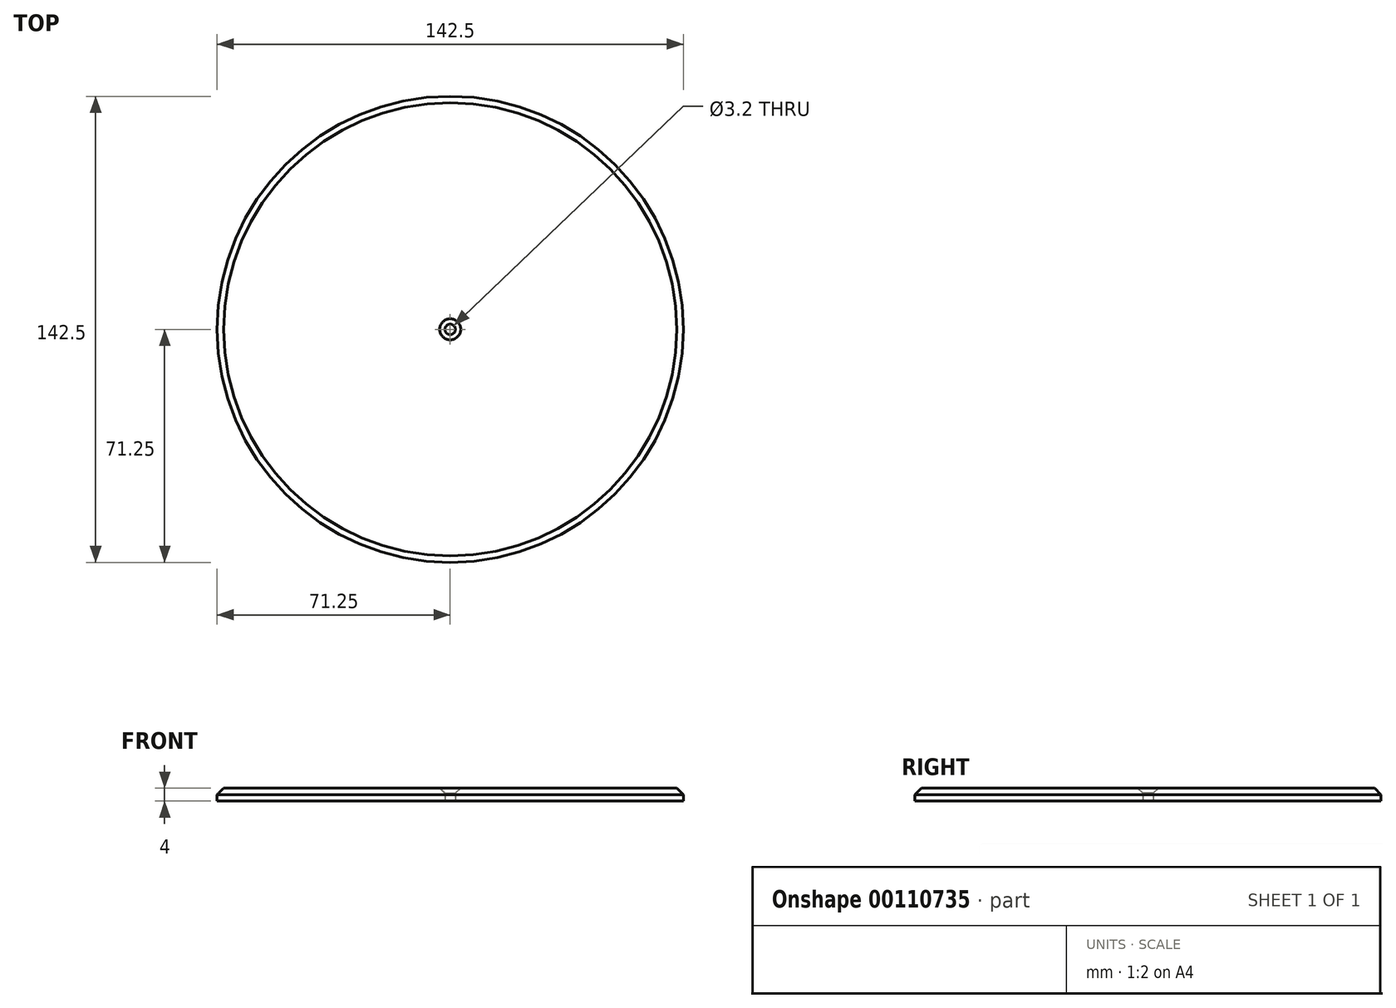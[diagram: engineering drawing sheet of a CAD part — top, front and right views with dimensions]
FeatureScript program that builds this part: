
annotation { "Feature Type Name" : "Feature", "Feature Type Description" : "" }
export const myFeature = defineFeature(function(context is Context, id is Id, definition is map)
    precondition{}
    {
        {
            var Q0;
            Q0=qCreatedBy(makeId("Front.planeOp"),FACE);
            var sketch = newSketch(context, id + "F0", { "sketchPlane" : qUnion([Q0])});
            skLineSegment(sketch, "E0", {"start": v(0, 0) * mm, "end": v(0, 45.75) * mm, "construction": true});
            skLineSegment(sketch, "E1", {"start": v(1.6, 0) * mm, "end": v(71.25, 0) * mm});
            skLineSegment(sketch, "E2", {"start": v(71.25, 0) * mm, "end": v(71.25, 2) * mm});
            skLineSegment(sketch, "E3", {"start": v(71.25, 2) * mm, "end": v(69.25, 4) * mm});
            skLineSegment(sketch, "E4", {"start": v(69.25, 4) * mm, "end": v(3.2, 4) * mm});
            skLineSegment(sketch, "E5", {"start": v(3.2, 4) * mm, "end": v(1.6, 2.4) * mm});
            skLineSegment(sketch, "E6", {"start": v(1.6, 2.4) * mm, "end": v(1.6, 0) * mm});
            skSolve(sketch);
        }
        {
            var Q0;
            Q0 = qSketchRegion(id + "F0", true);
            var Q1;
            Q1=sQuery(id+"F0.wireOp",EDGE,"E0");
            revolve(context, id + "F1", {"entities" : qUnion([Q0]), "axis" : qUnion([Q1]), "revolveType" : RevolveType.FULL});
        }
    });
